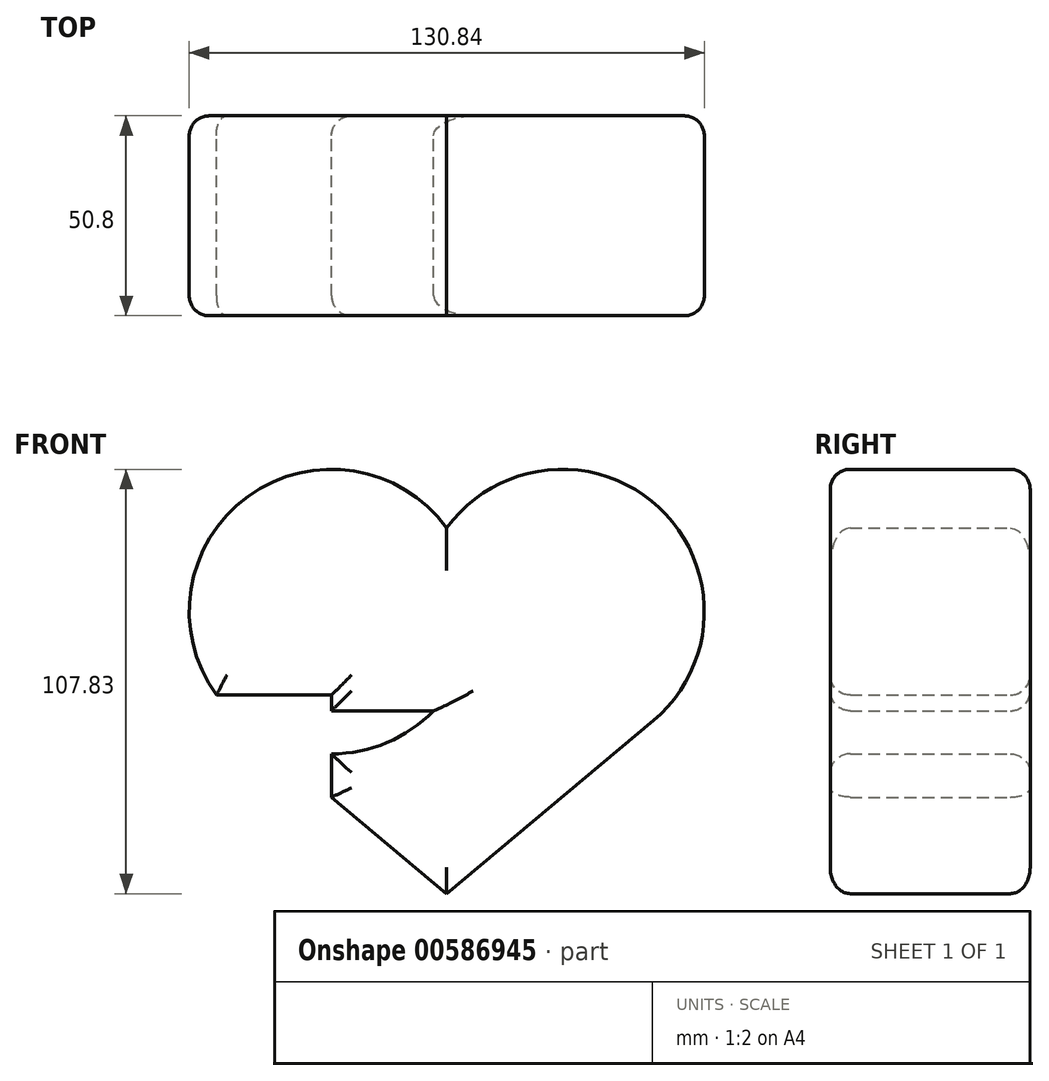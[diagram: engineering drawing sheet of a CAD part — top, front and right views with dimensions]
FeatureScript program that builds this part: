
annotation { "Feature Type Name" : "Feature", "Feature Type Description" : "" }
export const myFeature = defineFeature(function(context is Context, id is Id, definition is map)
    precondition{}
    {
        {
            var Q0;
            Q0=qCreatedBy(makeId("Front.planeOp"),FACE);
            var sketch = newSketch(context, id + "F0", { "sketchPlane" : qUnion([Q0])});
            skLineSegment(sketch, "E0", {"start": v(0, 46.45) * mm, "end": v(0, -46.45) * mm});
            skArc(sketch, "E1", {"start": v(0, 46.45) * mm, "mid": v(-53.93, 51.67) * mm, "end": v(-52.48, -2.5) * mm});
            skArc(sketch, "E2.MirrorCS", {"start": v(0, 46.45) * mm, "mid": v(53.93, 51.67) * mm, "end": v(52.48, -2.5) * mm});
            skLineSegment(sketch, "E3", {"start": v(0, -46.45) * mm, "end": v(-52.48, -2.5) * mm});
            skLineSegment(sketch, "E4", {"start": v(0, -46.45) * mm, "end": v(52.48, -2.5) * mm});
            skLineSegment(sketch, "E5", {"start": v(-29.27, 25.23) * mm, "end": v(-65.42, 25.23) * mm});
            skLineSegment(sketch, "E6", {"start": v(-29.27, 25.23) * mm, "end": v(0, 25.23) * mm});
            skLineSegment(sketch, "E7", {"start": v(-29.27, 25.23) * mm, "end": v(-29.27, 61.38) * mm});
            skLineSegment(sketch, "E8.MirrorCS", {"start": v(29.27, 25.23) * mm, "end": v(0, 25.23) * mm});
            skLineSegment(sketch, "E9.MirrorCS", {"start": v(29.27, 25.23) * mm, "end": v(65.42, 25.23) * mm});
            skLineSegment(sketch, "E10.MirrorCS", {"start": v(29.27, 25.23) * mm, "end": v(29.27, 61.38) * mm});
            skArc(sketch, "E11.MirrorCS", {"start": v(0, 4) * mm, "mid": v(53.93, -1.22) * mm, "end": v(52.48, 52.94) * mm});
            skLineSegment(sketch, "E12.MirrorCS", {"start": v(29.27, 25.23) * mm, "end": v(29.27, -10.93) * mm});
            skArc(sketch, "E13.MirrorCS", {"start": v(0, 4) * mm, "mid": v(-12.84, -6.98) * mm, "end": v(-29.27, -10.93) * mm});
            skLineSegment(sketch, "E14", {"start": v(-29.27, 0) * mm, "end": v(55.17, 0) * mm});
            skLineSegment(sketch, "E15", {"start": v(-29.27, 4) * mm, "end": v(-29.27, -21.93) * mm});
            skPoint(sketch, "E16.orphan", {"position": v(-29.27, -10.93) * mm});
            skArc(sketch, "E17.trimOffspring", {"start": v(-52.48, -2.5) * mm, "mid": v(-65.42, 25.23) * mm, "end": v(-52.48, 52.94) * mm});
            skLineSegment(sketch, "E18", {"start": v(0, 4) * mm, "end": v(-58.54, 4) * mm});
            skPoint(sketch, "E19.orphan", {"position": v(-55.17, 0) * mm});
            skLineSegment(sketch, "E20", {"start": v(-29.27, 25.23) * mm, "end": v(-29.27, 4) * mm});
            skSolve(sketch);
        }
        {
            var Q0;
            {var subQ4=sQuery(id+"F0.wireOp",EDGE,"E5");Q0=makeQuery(id+"F0.imprint","IMPRINT",FACE,{"disambiguationData":[TD([[makeQuery(id+"F0.imprint","IMPRINT",EDGE,{"derivedFrom":subQ4}),-1.0]])]});}
            var Q1;
            {var subQ0=sQuery(id+"F0.wireOp",EDGE,"E5");Q1=makeQuery(id+"F0.imprint","IMPRINT",FACE,{"disambiguationData":[TD([[makeQuery(id+"F0.imprint","IMPRINT",EDGE,{"derivedFrom":subQ0}),1.0]])]});}
            var Q2;
            {var subQ0=sQuery(id+"F0.wireOp",EDGE,"E6");Q2=makeQuery(id+"F0.imprint","IMPRINT",FACE,{"disambiguationData":[TD([[makeQuery(id+"F0.imprint","IMPRINT",EDGE,{"derivedFrom":subQ0}),-1.0]])]});}
            var Q3;
            {var subQ3=sQuery(id+"F0.wireOp",EDGE,"E6");Q3=makeQuery(id+"F0.imprint","IMPRINT",FACE,{"disambiguationData":[TD([[makeQuery(id+"F0.imprint","IMPRINT",EDGE,{"derivedFrom":subQ3}),1.0]])]});}
            var Q4;
            {var subQ3=sQuery(id+"F0.wireOp",EDGE,"E8.MirrorCS");Q4=makeQuery(id+"F0.imprint","IMPRINT",FACE,{"disambiguationData":[TD([[makeQuery(id+"F0.imprint","IMPRINT",EDGE,{"derivedFrom":subQ3}),-1.0]])]});}
            var Q5;
            {var subQ4=sQuery(id+"F0.wireOp",EDGE,"E9.MirrorCS");Q5=makeQuery(id+"F0.imprint","IMPRINT",FACE,{"disambiguationData":[TD([[makeQuery(id+"F0.imprint","IMPRINT",EDGE,{"derivedFrom":subQ4}),1.0]])]});}
            var Q6;
            {var subQ0=sQuery(id+"F0.wireOp",EDGE,"E9.MirrorCS");Q6=makeQuery(id+"F0.imprint","IMPRINT",FACE,{"disambiguationData":[TD([[makeQuery(id+"F0.imprint","IMPRINT",EDGE,{"derivedFrom":subQ0}),-1.0]])]});}
            var Q7;
            {var subQ1=sQuery(id+"F0.wireOp",EDGE,"E8.MirrorCS");Q7=makeQuery(id+"F0.imprint","IMPRINT",FACE,{"disambiguationData":[TD([[makeQuery(id+"F0.imprint","IMPRINT",EDGE,{"derivedFrom":subQ1}),1.0]])]});}
            var Q8;
            {var subQ1=sQuery(id+"F0.wireOp",EDGE,"E4");Q8=makeQuery(id+"F0.imprint","IMPRINT",FACE,{"disambiguationData":[TD([[makeQuery(id+"F0.imprint","IMPRINT",EDGE,{"derivedFrom":subQ1}),1.0]])]});}
            var Q9;
            {var subQ0=sQuery(id+"F0.wireOp",EDGE,"E15");var subQ1=sQuery(id+"F0.wireOp",EDGE,"E13.MirrorCS");var subQ2=makeQuery(id+"F0.imprint","INTERSECT",VERTEX,{"derivedFrom":[subQ1,subQ0]});Q9=makeQuery(id+"F0.imprint","IMPRINT",FACE,{"disambiguationData":[TD([[makeQuery(id+"F0.imprint","IMPRINT",EDGE,{"disambiguationData":[TD([[subQ2,1.0]])],"derivedFrom":subQ1}),1.0]])]});}
            var Q10;
            {var subQ3=sQuery(id+"F0.wireOp",EDGE,"E14");var subQ5=sQuery(id+"F0.wireOp",EDGE,"E15");var subQ6=makeQuery(id+"F0.imprint","INTERSECT",VERTEX,{"derivedFrom":[subQ3,subQ5]});Q10=makeQuery(id+"F0.imprint","IMPRINT",FACE,{"disambiguationData":[TD([[makeQuery(id+"F0.imprint","IMPRINT",EDGE,{"disambiguationData":[TD([[subQ6,-1.0]])],"derivedFrom":subQ3}),1.0]])]});}
            var Q11;
            {var subQ0=sQuery(id+"F0.wireOp",EDGE,"E15");var subQ1=sQuery(id+"F0.wireOp",EDGE,"E13.MirrorCS");var subQ2=makeQuery(id+"F0.imprint","INTERSECT",VERTEX,{"derivedFrom":[subQ1,subQ0]});Q11=makeQuery(id+"F0.imprint","IMPRINT",FACE,{"disambiguationData":[TD([[makeQuery(id+"F0.imprint","IMPRINT",EDGE,{"disambiguationData":[TD([[subQ2,1.0]])],"derivedFrom":subQ1}),-1.0]])]});}
            var Q12;
            {var subQ5=sQuery(id+"F0.wireOp",EDGE,"E3");var subQ7=sQuery(id+"F0.wireOp",EDGE,"E17.trimOffspring");var subQ8=makeQuery(id+"F0.imprint","INTERSECT",VERTEX,{"derivedFrom":[subQ5,subQ7]});Q12=makeQuery(id+"F0.imprint","IMPRINT",FACE,{"disambiguationData":[TD([[makeQuery(id+"F0.imprint","IMPRINT",EDGE,{"disambiguationData":[TD([[subQ8,1.0]])],"derivedFrom":subQ5}),-1.0]])]});}
            var Q13;
            {var subQ0=sQuery(id+"F0.wireOp",EDGE,"E11.MirrorCS");var subQ1=makeQuery(id+"F0.imprint","INTERSECT",VERTEX,{"derivedFrom":[sQuery(id+"F0.wireOp",EDGE,"E4"),subQ0]});Q13=makeQuery(id+"F0.imprint","IMPRINT",FACE,{"disambiguationData":[TD([[makeQuery(id+"F0.imprint","IMPRINT",EDGE,{"disambiguationData":[TD([[subQ1,1.0]])],"derivedFrom":subQ0}),1.0]])]});}
            var Q14;
            {var subQ0=sQuery(id+"F0.wireOp",EDGE,"E12.MirrorCS");var subQ1=sQuery(id+"F0.wireOp",EDGE,"E11.MirrorCS");var subQ2=makeQuery(id+"F0.imprint","INTERSECT",VERTEX,{"derivedFrom":[subQ1,subQ0]});Q14=makeQuery(id+"F0.imprint","IMPRINT",FACE,{"disambiguationData":[TD([[makeQuery(id+"F0.imprint","IMPRINT",EDGE,{"disambiguationData":[TD([[subQ2,1.0]])],"derivedFrom":subQ1}),1.0]])]});}
            var Q15;
            {var subQ1=sQuery(id+"F0.wireOp",EDGE,"E0");var subQ3=sQuery(id+"F0.wireOp",EDGE,"E14");var subQ4=makeQuery(id+"F0.imprint","INTERSECT",VERTEX,{"derivedFrom":[subQ1,subQ3]});Q15=makeQuery(id+"F0.imprint","IMPRINT",FACE,{"disambiguationData":[TD([[makeQuery(id+"F0.imprint","IMPRINT",EDGE,{"disambiguationData":[TD([[subQ4,-1.0]])],"derivedFrom":subQ3}),1.0]])]});}
            var Q16;
            {var subQ1=sQuery(id+"F0.wireOp",EDGE,"E0");var subQ3=sQuery(id+"F0.wireOp",EDGE,"E14");var subQ4=makeQuery(id+"F0.imprint","INTERSECT",VERTEX,{"derivedFrom":[subQ1,subQ3]});Q16=makeQuery(id+"F0.imprint","IMPRINT",FACE,{"disambiguationData":[TD([[makeQuery(id+"F0.imprint","IMPRINT",EDGE,{"disambiguationData":[TD([[subQ4,1.0]])],"derivedFrom":subQ3}),1.0]])]});}
            extrude(context, id + "F1", {"entities" : qUnion([Q0, Q1, Q2, Q3, Q4, Q5, Q6, Q7, Q8, Q9, Q10, Q11, Q12, Q13, Q14, Q15, Q16]), "endBound" : BoundingType.SYMMETRIC, "depth" : 50.8 * mm, "offsetDistance" : 25.4 * mm});
        }
        {
            var Q0;
            Q0=makeQuery(id+"F1.opExtrude","CAP_EDGE",EDGE,{"disambiguationData":[OSD([sQuery(id+"F0.wireOp",EDGE,"E2.MirrorCS"),sQuery(id+"F0.wireOp",EDGE,"E11.MirrorCS")])],"isStart":true});
            var Q1;
            Q1=makeQuery(id+"F1.opExtrude","CAP_EDGE",EDGE,{"disambiguationData":[OSD([sQuery(id+"F0.wireOp",EDGE,"E4")])],"isStart":true});
            var Q2;
            Q2=makeQuery(id+"F1.opExtrude","CAP_FACE",FACE,{"disambiguationData":[OSD([sQuery(id+"F0.wireOp",EDGE,"E1"),sQuery(id+"F0.wireOp",EDGE,"E2.MirrorCS"),sQuery(id+"F0.wireOp",EDGE,"E3"),sQuery(id+"F0.wireOp",EDGE,"E4"),sQuery(id+"F0.wireOp",EDGE,"E11.MirrorCS"),sQuery(id+"F0.wireOp",EDGE,"E17.trimOffspring")])],"isStart":true});
            var Q3;
            Q3=makeQuery(id+"F1.opExtrude","CAP_FACE",FACE,{"disambiguationData":[OSD([sQuery(id+"F0.wireOp",EDGE,"E1"),sQuery(id+"F0.wireOp",EDGE,"E2.MirrorCS"),sQuery(id+"F0.wireOp",EDGE,"E3"),sQuery(id+"F0.wireOp",EDGE,"E4"),sQuery(id+"F0.wireOp",EDGE,"E11.MirrorCS"),sQuery(id+"F0.wireOp",EDGE,"E17.trimOffspring")])],"isStart":false});
            fillet(context, id + "F2", {"entities" : qUnion([Q0, Q1, Q2, Q3]), "radius" : 5.08 * mm, "tangentPropagation" : true, "allowEdgeOverflow" : false});
        }
    });
